# Revit family: Romerska ringar
name_source: partatom
category: Generic Models
units: mm (PartAtom-declared; Revit-internal decimal feet)

## family parameters
Always vertical = Yes
Can host rebar = No
Cut with Voids When Loaded = No
Part Type = Normal
Room Calculation Point = No
Round Connector Dimension = Use Diameter
Shared = No
Work Plane-Based = No

## types (4) — shared parameters
1 par = Yes
Height = 7000 mm  [stored 22.9659 ft]
Height_to_wheel = 6880 mm
Manufacturer = Saxi Vägg AB
URL = www.saxi.se
langd_rep = 6410 mm  [stored 21.0302 ft]
langd_wire = 4250 mm
langd_wire_inf = 5400 mm  [stored 17.7165 ft]

## per-type parameters (varying)
| type | 2 par | 3 par | 4 par | INF_1 | INF_2 | INF_3 | INF_4 | Length_straight | NO_ROPES | beam_length |
| Saxi Romerska ringar 1 par | No | No | No | Yes | No | No | No | 2550 mm  [stored 8.36614 ft] | 4 | 2604 mm  [stored 8.54331 ft] |
| Saxi Romerska ringar 4 par | Yes | Yes | Yes | No | No | No | Yes | 3297 mm  [stored 10.8169 ft] | 5 | 9000 mm |
| Saxi Romerska ringar 3 par | Yes | Yes | No | No | No | Yes | No | 3947 mm  [stored 12.9495 ft] | 6 | 6931 mm  [stored 22.7395 ft] |
| Saxi Romerska ringar 2 par | Yes | No | No | No | Yes | No | No | 4335 mm  [stored 14.2224 ft] | 7 | 5000 mm  [stored 16.4042 ft] |

note: column(s) folded — value = type name in every type: Model

note: [stored X ft] marks values corroborated as IEEE doubles in the binary element streams (Revit-internal decimal feet)

## geometry (parser evidence)
native form markers: Sweep x73
no freeform markers — native parametric forms only
